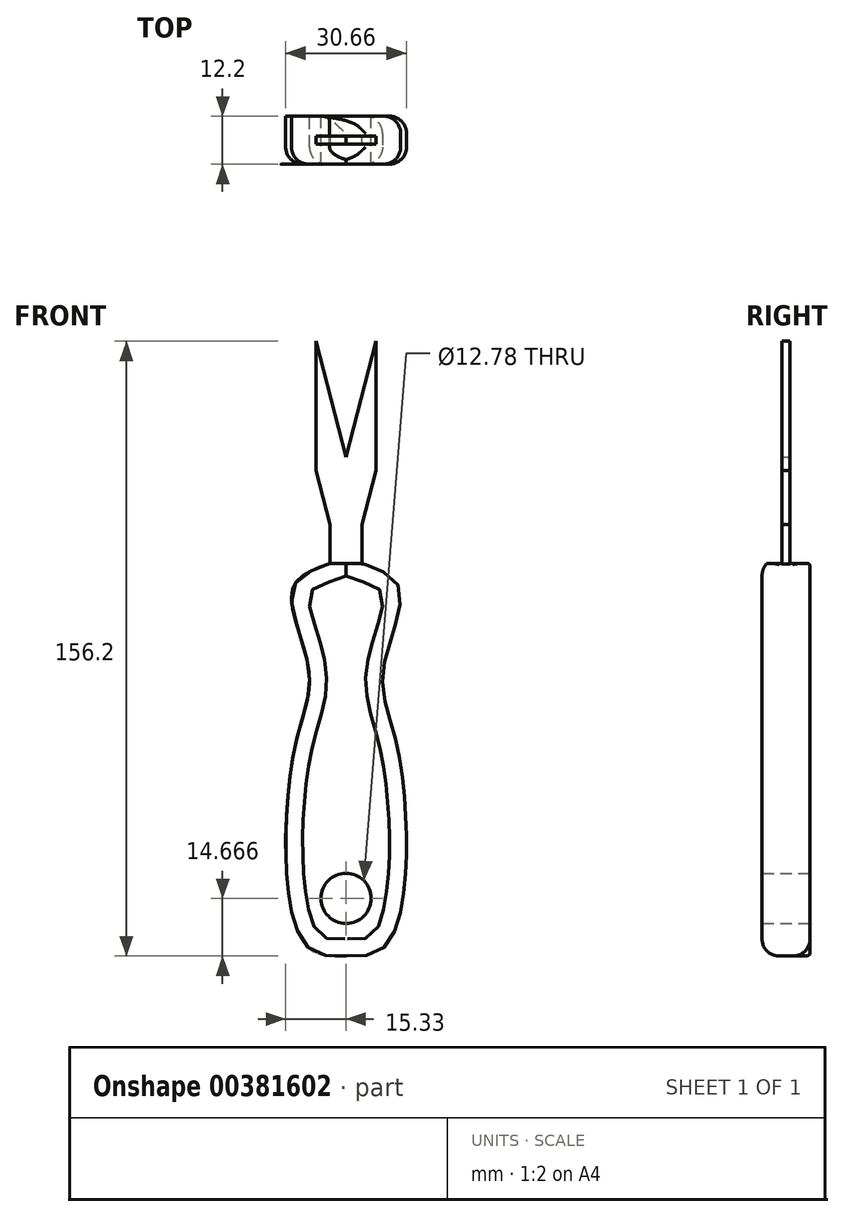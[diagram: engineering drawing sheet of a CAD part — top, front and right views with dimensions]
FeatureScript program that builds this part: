
annotation { "Feature Type Name" : "Feature", "Feature Type Description" : "" }
export const myFeature = defineFeature(function(context is Context, id is Id, definition is map)
    precondition{}
    {
        {
            var Q0;
            Q0=qCreatedBy(makeId("Front.planeOp"),FACE);
            var sketch = newSketch(context, id + "F0", { "sketchPlane" : qUnion([Q0])});
            skLineSegment(sketch, "E0", {"start": v(0, 57.45) * mm, "end": v(-7.62, 86.87) * mm});
            skLineSegment(sketch, "E1", {"start": v(-7.62, 86.87) * mm, "end": v(-7.62, 54.01) * mm});
            skLineSegment(sketch, "E2", {"start": v(-7.62, 54.01) * mm, "end": v(-4.07, 40.29) * mm});
            skLineSegment(sketch, "E3", {"start": v(-4.07, 40.29) * mm, "end": v(-4.07, 30.32) * mm});
            skFitSpline(sketch, "E4", {"points": [v(-4.07, 30.32) * mm, v(-12.97, 27.27) * mm, v(-11.82, 8.55) * mm, v(-10.16, 0) * mm, v(-10.8, -8.65) * mm, v(-11.43, -74.74) * mm, v(0, -82) * mm, v(0, -83.15) * mm], "startDerivative": vector(-93.6, -4.08) * mm, "endDerivative": vector(-11.64, -30.24) * mm});
            skLineSegment(sketch, "E5.MirrorCS", {"start": v(0, 57.45) * mm, "end": v(7.62, 86.87) * mm});
            skLineSegment(sketch, "E6.MirrorCS", {"start": v(7.62, 86.87) * mm, "end": v(7.62, 54.01) * mm});
            skLineSegment(sketch, "E7.MirrorCS", {"start": v(7.62, 54.01) * mm, "end": v(4.07, 40.29) * mm});
            skLineSegment(sketch, "E8.MirrorCS", {"start": v(4.07, 40.29) * mm, "end": v(4.07, 30.32) * mm});
            skFitSpline(sketch, "E9.MirrorCS", {"points": [v(4.07, 30.32) * mm, v(12.97, 27.27) * mm, v(11.82, 8.55) * mm, v(10.16, 0) * mm, v(10.8, -8.65) * mm, v(11.43, -74.74) * mm, v(0, -82) * mm, v(0, -83.15) * mm], "startDerivative": vector(93.6, -4.08) * mm, "endDerivative": vector(11.64, -30.24) * mm});
            skLineSegment(sketch, "E10", {"start": v(-4.07, 30.32) * mm, "end": v(4.07, 30.32) * mm});
            skSolve(sketch);
        }
        {
            var Q0;
            Q0=makeQuery(id+"F0.imprint","IMPRINT",FACE,{"disambiguationData":[TD([[makeQuery(id+"F0.imprint","IMPRINT",EDGE,{"derivedFrom":sQuery(id+"F0.wireOp",EDGE,"E0")}),1.0]])]});
            extrude(context, id + "F1", {"entities" : qUnion([Q0]), "endBound" : BoundingType.SYMMETRIC, "depth" : 2.03 * mm});
        }
        {
            var Q0;
            Q0=qCreatedBy(makeId("Front.planeOp"),FACE);
            var sketch = newSketch(context, id + "F2", { "sketchPlane" : qUnion([Q0])});
            skFitSpline(sketch, "E11", {"points": [v(-4.2, 30.37) * mm, v(-13.63, 23.82) * mm, v(-9.44, 3.37) * mm, v(-13.37, -18.13) * mm, v(-11.01, -65.6) * mm, v(0, -69.26) * mm], "startDerivative": vector(-85.92, -29.78) * mm, "endDerivative": vector(83.78, 3.2) * mm});
            skFitSpline(sketch, "E12.MirrorCS", {"points": [v(4.2, 30.37) * mm, v(13.63, 23.82) * mm, v(9.44, 3.37) * mm, v(13.37, -18.13) * mm, v(11.01, -65.6) * mm, v(0, -69.26) * mm], "startDerivative": vector(85.92, -29.78) * mm, "endDerivative": vector(-83.78, 3.2) * mm});
            skLineSegment(sketch, "E13", {"start": v(-4.2, 30.37) * mm, "end": v(4.2, 30.37) * mm});
            skCircle(sketch, "E14", {"center": v(0, -54.66) * mm, "radius": 6.4 * mm});
            skSolve(sketch);
        }
        {
            var Q0;
            Q0 = qSketchRegion(id + "F2", true);
            extrude(context, id + "F3", {"entities" : qUnion([Q0]), "operationType" : NewBodyOperationType.ADD, "endBound" : BoundingType.SYMMETRIC, "depth" : 12.2 * mm});
        }
        {
            var Q0;
            Q0=makeQuery(id+"F3.opExtrude","CAP_EDGE",EDGE,{"disambiguationData":[OSD([sQuery(id+"F2.wireOp",EDGE,"E12.MirrorCS")])],"isStart":false});
            var Q1;
            Q1=makeQuery(id+"F3.opExtrude","CAP_EDGE",EDGE,{"disambiguationData":[OSD([sQuery(id+"F2.wireOp",EDGE,"E11")])],"isStart":false});
            var Q2;
            Q2=makeQuery(id+"F3.opExtrude","SWEPT_FACE",FACE,{"disambiguationData":[OSD([sQuery(id+"F2.wireOp",EDGE,"E12.MirrorCS")])]});
            fillet(context, id + "F4", {"entities" : qUnion([Q0, Q1, Q2]), "radius" : 4.32 * mm, "tangentPropagation" : true, "allowEdgeOverflow" : false});
        }
    });
